# Revit family: Axis-Jet-СI
name_source: partatom
category: Оборудование
units: mm (PartAtom-declared; Revit-internal decimal feet)

## family parameters
Всегда вертикально = Да
Классификация = Нет
На основе рабочей плоскости = Нет
Общий = Нет
При загрузке вырезать с полостями = Нет
Размер круглого соединителя = Использовать диаметр
Тип детали = Нормальный
Точка принадлежности помещению = Нет

## types (126) — shared parameters
00_20_Manufacturer = BLAUBERG
00_20_Name = Jet axial fan
Casing Material = Metal, painted, grey, matt RAL 7040
E1 = 830 мм
Frequency = 50 Гц
Load Classification = HVAC
Maintenance zone material = <По категории>
Number of Fase = 3
Thrust = 0.00 Н
Voltage = 400 В
Изготовитель = BLAUBERG
zero-valued in all types: Отметка по умолчанию

## per-type parameters (varying)
- Axis-Jet-СI-315-2-U: 00_20_Type=Axis-Jet-СI-315-2-U; A=302 мм; A1=342 мм; B=355 мм; D=414 мм; D1=394 мм; D2=294 мм; Dy=315 мм; H=425 мм; Height=425 мм; L=1654 мм; L1=1763 мм; Length=1763 мм; Maximum Air Flow=4520.0 м³/ч; Motor=Motor : Motor_315; Power=550 Вт; R=207 мм; Type R=Нет; Weight=40.00 кг; Width=414 мм; d1=9 мм; dn=319 мм; k=40 мм; l=109 мм; r=158 мм; t=104 мм
- Axis-Jet-CI-630-2/4-U: 00_20_Type=Axis-Jet-CI-630-2/4-U; A=550 мм; A1=600 мм; B=710 мм; D=733 мм; D1=713 мм; D2=613 мм; Dy=630 мм; H=748 мм; Height=748 мм; L=2193 мм; L1=2357 мм; Length=2357 мм; Maximum Air Flow=31500.0 м³/ч; Motor=Motor : Motor_630; Power=12000 Вт; R=367 мм; Type R=Нет; Weight=245.00 кг; Width=733 мм; d1=13 мм; dn=634 мм; k=50 мм; l=164 мм; r=315 мм; t=183 мм
- Axis-Jet-СI-315-2-R: 00_20_Type=Axis-Jet-СI-315-2-R; A=302 мм; A1=342 мм; B=355 мм; D=414 мм; D1=394 мм; D2=294 мм; Dy=315 мм; H=425 мм; Height=425 мм; L=1654 мм; L1=1763 мм; Length=1872 мм; Maximum Air Flow=4190.0 м³/ч; Motor=Motor : Motor_315; Power=550 Вт; R=207 мм; Type R=Да; Weight=40.00 кг; Width=414 мм; d1=9 мм; dn=319 мм; k=40 мм; l=109 мм; r=158 мм; t=104 мм
- Axis-Jet-СI-355-2-U: 00_20_Type=Axis-Jet-СI-355-2-U; A=302 мм; A1=342 мм; B=420 мм; D=467 мм; D1=447 мм; D2=347 мм; Dy=355 мм; H=482 мм; Height=482 мм; L=1954 мм; L1=2079 мм; Length=2079 мм; Maximum Air Flow=5830.0 м³/ч; Motor=Motor : Motor_355; Power=750 Вт; R=234 мм; Type R=Нет; Weight=50.00 кг; Width=467 мм; d1=9 мм; dn=359 мм; k=40 мм; l=125 мм; r=178 мм; t=117 мм
- Axis-Jet-СI-355-2-R: 00_20_Type=Axis-Jet-СI-355-2-R; A=302 мм; A1=342 мм; B=420 мм; D=467 мм; D1=447 мм; D2=347 мм; Dy=355 мм; H=482 мм; Height=482 мм; L=1954 мм; L1=2079 мм; Length=2204 мм; Maximum Air Flow=5810.0 м³/ч; Motor=Motor : Motor_355; Power=1100 Вт; R=234 мм; Type R=Да; Weight=50.00 кг; Width=467 мм; d1=9 мм; dn=359 мм; k=40 мм; l=125 мм; r=178 мм; t=117 мм
- Axis-Jet-СI-400-2-U: 00_20_Type=Axis-Jet-СI-400-2-U; A=351 мм; A1=401 мм; B=460 мм; D=515 мм; D1=495 мм; D2=395 мм; Dy=400 мм; H=525 мм; Height=525 мм; L=2004 мм; L1=2129 мм; Length=2129 мм; Maximum Air Flow=8500.0 м³/ч; Motor=Motor : Motor_400; Power=1100 Вт; R=258 мм; Type R=Нет; Weight=65.00 кг; Width=515 мм; d1=13 мм; dn=404 мм; k=50 мм; l=125 мм; r=200 мм; t=129 мм
- Axis-Jet-СI-400-2-R: 00_20_Type=Axis-Jet-СI-400-2-R; A=351 мм; A1=401 мм; B=460 мм; D=515 мм; D1=495 мм; D2=395 мм; Dy=400 мм; H=525 мм; Height=525 мм; L=2004 мм; L1=2129 мм; Length=2254 мм; Maximum Air Flow=8290.0 м³/ч; Motor=Motor : Motor_400; Power=1500 Вт; R=258 мм; Type R=Да; Weight=65.00 кг; Width=515 мм; d1=13 мм; dn=404 мм; k=50 мм; l=125 мм; r=200 мм; t=129 мм
- Axis-Jet-СI-450-2-U: 00_20_Type=Axis-Jet-СI-450-2-U; A=351 мм; A1=401 мм; B=500 мм; D=565 мм; D1=545 мм; D2=445 мм; Dy=450 мм; H=575 мм; Height=575 мм; L=2004 мм; L1=2129 мм; Length=2129 мм; Maximum Air Flow=10400.0 м³/ч; Motor=Motor : Motor_450; Power=1500 Вт; R=283 мм; Type R=Нет; Weight=85.00 кг; Width=565 мм; d1=13 мм; dn=454 мм; k=50 мм; l=125 мм; r=225 мм; t=141 мм
- Axis-Jet-СI-450-2-R: 00_20_Type=Axis-Jet-СI-450-2-R; A=351 мм; A1=401 мм; B=500 мм; D=565 мм; D1=545 мм; D2=445 мм; Dy=450 мм; H=575 мм; Height=575 мм; L=2004 мм; L1=2129 мм; Length=2254 мм; Maximum Air Flow=9280.0 м³/ч; Motor=Motor : Motor_450; Power=1500 Вт; R=283 мм; Type R=Да; Weight=85.00 кг; Width=565 мм; d1=13 мм; dn=454 мм; k=50 мм; l=125 мм; r=225 мм; t=141 мм
- Axis-Jet-СI-500-2/4-U: 00_20_Type=Axis-Jet-СI-500-2/4-U; A=371 мм; A1=421 мм; B=580 мм; D=603 мм; D1=583 мм; D2=483 мм; Dy=500 мм; H=620 мм; Height=620 мм; L=2004 мм; L1=2145 мм; Length=2145 мм; Maximum Air Flow=16200.0 м³/ч; Motor=Motor : Motor_500; Power=3100 Вт; R=302 мм; Type R=Нет; Weight=110.00 кг; Width=603 мм; d1=13 мм; dn=504 мм; k=50 мм; l=141 мм; r=250 мм; t=151 мм
- Axis-Jet-CI-500-2/4-R: 00_20_Type=Axis-Jet-CI-500-2/4-R; A=371 мм; A1=421 мм; B=580 мм; D=603 мм; D1=583 мм; D2=483 мм; Dy=500 мм; H=620 мм; Height=620 мм; L=2004 мм; L1=2145 мм; Length=2286 мм; Maximum Air Flow=14500.0 м³/ч; Motor=Motor : Motor_500; Power=3100 Вт; R=302 мм; Type R=Да; Weight=110.00 кг; Width=603 мм; d1=13 мм; dn=504 мм; k=50 мм; l=141 мм; r=250 мм; t=151 мм
- Axis-Jet-CI-560-2/4-U: 00_20_Type=Axis-Jet-CI-560-2/4-U; A=446 мм; A1=496 мм; B=620 мм; D=663 мм; D1=643 мм; D2=543 мм; Dy=560 мм; H=678 мм; Height=678 мм; L=2093 мм; L1=2247 мм; Length=2247 мм; Maximum Air Flow=20200.0 м³/ч; Motor=Motor : Motor_560; Power=4400 Вт; R=332 мм; Type R=Нет; Weight=155.00 кг; Width=663 мм; d1=13 мм; dn=564 мм; k=50 мм; l=154 мм; r=280 мм; t=166 мм
- Axis-Jet-CI-560-2/4-R: 00_20_Type=Axis-Jet-CI-560-2/4-R; A=446 мм; A1=496 мм; B=620 мм; D=663 мм; D1=643 мм; D2=543 мм; Dy=560 мм; H=678 мм; Height=678 мм; L=2093 мм; L1=2247 мм; Length=2401 мм; Maximum Air Flow=16800.0 м³/ч; Motor=Motor : Motor_560; Power=4400 Вт; R=332 мм; Type R=Да; Weight=155.00 кг; Width=663 мм; d1=13 мм; dn=564 мм; k=50 мм; l=154 мм; r=280 мм; t=166 мм
- Axis-Jet-CI-630-2/4-R: 00_20_Type=Axis-Jet-CI-630-2/4-R; A=550 мм; A1=600 мм; B=710 мм; D=733 мм; D1=713 мм; D2=613 мм; Dy=630 мм; H=748 мм; Height=748 мм; L=2193 мм; L1=2357 мм; Length=2521 мм; Maximum Air Flow=26700.0 м³/ч; Motor=Motor : Motor_630; Power=12000 Вт; R=367 мм; Type R=Да; Weight=245.00 кг; Width=733 мм; d1=13 мм; dn=634 мм; k=50 мм; l=164 мм; r=315 мм; t=183 мм
- Axis-Jet-СI-315-2-U-300/2: 00_20_Type=Axis-Jet-СI-315-2-U-300/2; A=302 мм; A1=342 мм; B=355 мм; D=414 мм; D1=394 мм; D2=294 мм; Dy=315 мм; H=425 мм; Height=425 мм; L=1654 мм; L1=1763 мм; Length=1763 мм; Maximum Air Flow=4520.0 м³/ч; Motor=Motor : Motor_315; Power=550 Вт; R=207 мм; Type R=Нет; Weight=40.00 кг; Width=414 мм; d1=9 мм; dn=319 мм; k=40 мм; l=109 мм; r=158 мм; t=104 мм
- Axis-Jet-СI-315-2-U-400/2: 00_20_Type=Axis-Jet-СI-315-2-U-400/2; A=302 мм; A1=342 мм; B=355 мм; D=414 мм; D1=394 мм; D2=294 мм; Dy=315 мм; H=425 мм; Height=425 мм; L=1654 мм; L1=1763 мм; Length=1763 мм; Maximum Air Flow=3250.0 м³/ч; Motor=Motor : Motor_315; Power=550 Вт; R=207 мм; Type R=Нет; Weight=40.00 кг; Width=414 мм; d1=9 мм; dn=319 мм; k=40 мм; l=109 мм; r=158 мм; t=104 мм
- Axis-Jet-СI-315M-2-U: 00_20_Type=Axis-Jet-СI-315M-2-U; A=302 мм; A1=342 мм; B=355 мм; D=414 мм; D1=394 мм; D2=294 мм; Dy=315 мм; H=425 мм; Height=425 мм; L=1654 мм; L1=1763 мм; Length=1763 мм; Maximum Air Flow=4990.0 м³/ч; Motor=Motor : Motor_315; Power=750 Вт; R=207 мм; Type R=Нет; Weight=40.00 кг; Width=414 мм; d1=9 мм; dn=319 мм; k=40 мм; l=109 мм; r=158 мм; t=104 мм
- Axis-Jet-СI-315M-2-U-300/2: 00_20_Type=Axis-Jet-СI-315M-2-U-300/2; A=302 мм; A1=342 мм; B=355 мм; D=414 мм; D1=394 мм; D2=294 мм; Dy=315 мм; H=425 мм; Height=425 мм; L=1654 мм; L1=1763 мм; Length=1763 мм; Maximum Air Flow=4990.0 м³/ч; Motor=Motor : Motor_315; Power=750 Вт; R=207 мм; Type R=Нет; Weight=40.00 кг; Width=414 мм; d1=9 мм; dn=319 мм; k=40 мм; l=109 мм; r=158 мм; t=104 мм
- Axis-Jet-СI-315M-2-U-400/2: 00_20_Type=Axis-Jet-СI-315M-2-U-400/2; A=302 мм; A1=342 мм; B=355 мм; D=414 мм; D1=394 мм; D2=294 мм; Dy=315 мм; H=425 мм; Height=425 мм; L=1654 мм; L1=1763 мм; Length=1763 мм; Maximum Air Flow=3590.0 м³/ч; Motor=Motor : Motor_315; Power=750 Вт; R=207 мм; Type R=Нет; Weight=40.00 кг; Width=414 мм; d1=9 мм; dn=319 мм; k=40 мм; l=109 мм; r=158 мм; t=104 мм
- Axis-Jet-СI-315-2/4-U: 00_20_Type=Axis-Jet-СI-315-2/4-U; A=302 мм; A1=342 мм; B=355 мм; D=414 мм; D1=394 мм; D2=294 мм; Dy=315 мм; H=425 мм; Height=425 мм; L=1654 мм; L1=1763 мм; Length=1763 мм; Maximum Air Flow=4520.0 м³/ч; Motor=Motor : Motor_315; Power=550 Вт; R=207 мм; Type R=Нет; Weight=40.00 кг; Width=414 мм; d1=9 мм; dn=319 мм; k=40 мм; l=109 мм; r=158 мм; t=104 мм
- Axis-Jet-СI-315-2/4-U-300/2: 00_20_Type=Axis-Jet-СI-315-2/4-U-300/2; A=302 мм; A1=342 мм; B=355 мм; D=414 мм; D1=394 мм; D2=294 мм; Dy=315 мм; H=425 мм; Height=425 мм; L=1654 мм; L1=1763 мм; Length=1763 мм; Maximum Air Flow=4520.0 м³/ч; Motor=Motor : Motor_315; Power=550 Вт; R=207 мм; Type R=Нет; Weight=40.00 кг; Width=414 мм; d1=9 мм; dn=319 мм; k=40 мм; l=109 мм; r=158 мм; t=104 мм
- Axis-Jet-СI-315-2/4-U-400/2: 00_20_Type=Axis-Jet-СI-315-2/4-U-400/2; A=302 мм; A1=342 мм; B=355 мм; D=414 мм; D1=394 мм; D2=294 мм; Dy=315 мм; H=425 мм; Height=425 мм; L=1654 мм; L1=1763 мм; Length=1763 мм; Maximum Air Flow=3250.0 м³/ч; Motor=Motor : Motor_315; Power=550 Вт; R=207 мм; Type R=Нет; Weight=40.00 кг; Width=414 мм; d1=9 мм; dn=319 мм; k=40 мм; l=109 мм; r=158 мм; t=104 мм
- Axis-Jet-СI-315M-2/4-U: 00_20_Type=Axis-Jet-СI-315M-2/4-U; A=302 мм; A1=342 мм; B=355 мм; D=414 мм; D1=394 мм; D2=294 мм; Dy=315 мм; H=425 мм; Height=425 мм; L=1654 мм; L1=1763 мм; Length=1763 мм; Maximum Air Flow=4990.0 м³/ч; Motor=Motor : Motor_315; Power=800 Вт; R=207 мм; Type R=Нет; Weight=40.00 кг; Width=414 мм; d1=9 мм; dn=319 мм; k=40 мм; l=109 мм; r=158 мм; t=104 мм
- Axis-Jet-СI-315M-2/4-U-300/2: 00_20_Type=Axis-Jet-СI-315M-2/4-U-300/2; A=302 мм; A1=342 мм; B=355 мм; D=414 мм; D1=394 мм; D2=294 мм; Dy=315 мм; H=425 мм; Height=425 мм; L=1654 мм; L1=1763 мм; Length=1763 мм; Maximum Air Flow=4990.0 м³/ч; Motor=Motor : Motor_315; Power=800 Вт; R=207 мм; Type R=Нет; Weight=40.00 кг; Width=414 мм; d1=9 мм; dn=319 мм; k=40 мм; l=109 мм; r=158 мм; t=104 мм
- Axis-Jet-СI-315M-2/4-U-400/2: 00_20_Type=Axis-Jet-СI-315M-2/4-U-400/2; A=302 мм; A1=342 мм; B=355 мм; D=414 мм; D1=394 мм; D2=294 мм; Dy=315 мм; H=425 мм; Height=425 мм; L=1654 мм; L1=1763 мм; Length=1763 мм; Maximum Air Flow=3590.0 м³/ч; Motor=Motor : Motor_315; Power=800 Вт; R=207 мм; Type R=Нет; Weight=40.00 кг; Width=414 мм; d1=9 мм; dn=319 мм; k=40 мм; l=109 мм; r=158 мм; t=104 мм
- Axis-Jet-СI-315-2-R-300/2: 00_20_Type=Axis-Jet-СI-315-2-R-300/2; A=302 мм; A1=342 мм; B=355 мм; D=414 мм; D1=394 мм; D2=294 мм; Dy=315 мм; H=425 мм; Height=425 мм; L=1654 мм; L1=1763 мм; Length=1872 мм; Maximum Air Flow=4190.0 м³/ч; Motor=Motor : Motor_315; Power=550 Вт; R=207 мм; Type R=Да; Weight=40.00 кг; Width=414 мм; d1=9 мм; dn=319 мм; k=40 мм; l=109 мм; r=158 мм; t=104 мм
- Axis-Jet-СI-315-2-R-400/2: 00_20_Type=Axis-Jet-СI-315-2-R-400/2; A=302 мм; A1=342 мм; B=355 мм; D=414 мм; D1=394 мм; D2=294 мм; Dy=315 мм; H=425 мм; Height=425 мм; L=1654 мм; L1=1763 мм; Length=1872 мм; Maximum Air Flow=3010.0 м³/ч; Motor=Motor : Motor_315; Power=550 Вт; R=207 мм; Type R=Да; Weight=40.00 кг; Width=414 мм; d1=9 мм; dn=319 мм; k=40 мм; l=109 мм; r=158 мм; t=104 мм
- Axis-Jet-СI-315-2/4-R-300/2: 00_20_Type=Axis-Jet-СI-315-2/4-R-300/2; A=302 мм; A1=342 мм; B=355 мм; D=414 мм; D1=394 мм; D2=294 мм; Dy=315 мм; H=425 мм; Height=425 мм; L=1654 мм; L1=1763 мм; Length=1872 мм; Maximum Air Flow=4180.0 м³/ч; Motor=Motor : Motor_315; Power=550 Вт; R=207 мм; Type R=Да; Weight=40.00 кг; Width=414 мм; d1=9 мм; dn=319 мм; k=40 мм; l=109 мм; r=158 мм; t=104 мм
- Axis-Jet-СI-315-2/4-R-400/2: 00_20_Type=Axis-Jet-СI-315-2/4-R-400/2; A=302 мм; A1=342 мм; B=355 мм; D=414 мм; D1=394 мм; D2=294 мм; Dy=315 мм; H=425 мм; Height=425 мм; L=1654 мм; L1=1763 мм; Length=1872 мм; Maximum Air Flow=3010.0 м³/ч; Motor=Motor : Motor_315; Power=550 Вт; R=207 мм; Type R=Да; Weight=40.00 кг; Width=414 мм; d1=9 мм; dn=319 мм; k=40 мм; l=109 мм; r=158 мм; t=104 мм
- Axis-Jet-СI-355-2-U-300/2: 00_20_Type=Axis-Jet-СI-355-2-U-300/2; A=302 мм; A1=342 мм; B=420 мм; D=467 мм; D1=447 мм; D2=347 мм; Dy=355 мм; H=482 мм; Height=482 мм; L=1954 мм; L1=2079 мм; Length=2079 мм; Maximum Air Flow=5830.0 м³/ч; Motor=Motor : Motor_355; Power=750 Вт; R=234 мм; Type R=Нет; Weight=50.00 кг; Width=467 мм; d1=9 мм; dn=359 мм; k=40 мм; l=125 мм; r=178 мм; t=117 мм
- Axis-Jet-СI-355-2-U-400/2: 00_20_Type=Axis-Jet-СI-355-2-U-400/2; A=302 мм; A1=342 мм; B=420 мм; D=467 мм; D1=447 мм; D2=347 мм; Dy=355 мм; H=482 мм; Height=482 мм; L=1954 мм; L1=2079 мм; Length=2079 мм; Maximum Air Flow=4880.0 м³/ч; Motor=Motor : Motor_355; Power=750 Вт; R=234 мм; Type R=Нет; Weight=50.00 кг; Width=467 мм; d1=9 мм; dn=359 мм; k=40 мм; l=125 мм; r=178 мм; t=117 мм
- Axis-Jet-СI-355M-2-U: 00_20_Type=Axis-Jet-СI-355M-2-U; A=302 мм; A1=342 мм; B=420 мм; D=467 мм; D1=447 мм; D2=347 мм; Dy=355 мм; H=482 мм; Height=482 мм; L=1954 мм; L1=2079 мм; Length=2079 мм; Maximum Air Flow=6740.0 м³/ч; Motor=Motor : Motor_355; Power=11000 Вт; R=234 мм; Type R=Нет; Weight=50.00 кг; Width=467 мм; d1=9 мм; dn=359 мм; k=40 мм; l=125 мм; r=178 мм; t=117 мм
- Axis-Jet-СI-355M-2-U-300/2: 00_20_Type=Axis-Jet-СI-355M-2-U-300/2; A=302 мм; A1=342 мм; B=420 мм; D=467 мм; D1=447 мм; D2=347 мм; Dy=355 мм; H=482 мм; Height=482 мм; L=1954 мм; L1=2079 мм; Length=2079 мм; Maximum Air Flow=6740.0 м³/ч; Motor=Motor : Motor_355; Power=11000 Вт; R=234 мм; Type R=Нет; Weight=50.00 кг; Width=467 мм; d1=9 мм; dn=359 мм; k=40 мм; l=125 мм; r=178 мм; t=117 мм
- Axis-Jet-СI-355M-2-U-400/2: 00_20_Type=Axis-Jet-СI-355M-2-U-400/2; A=302 мм; A1=342 мм; B=420 мм; D=467 мм; D1=447 мм; D2=347 мм; Dy=355 мм; H=482 мм; Height=482 мм; L=1954 мм; L1=2079 мм; Length=2079 мм; Maximum Air Flow=5360.0 м³/ч; Motor=Motor : Motor_355; Power=11000 Вт; R=234 мм; Type R=Нет; Weight=50.00 кг; Width=467 мм; d1=9 мм; dn=359 мм; k=40 мм; l=125 мм; r=178 мм; t=117 мм
- Axis-Jet-СI-355-2/4-U: 00_20_Type=Axis-Jet-СI-355-2/4-U; A=302 мм; A1=342 мм; B=420 мм; D=467 мм; D1=447 мм; D2=347 мм; Dy=355 мм; H=482 мм; Height=482 мм; L=1954 мм; L1=2079 мм; Length=2079 мм; Maximum Air Flow=5830.0 м³/ч; Motor=Motor : Motor_355; Power=800 Вт; R=234 мм; Type R=Нет; Weight=50.00 кг; Width=467 мм; d1=9 мм; dn=359 мм; k=40 мм; l=125 мм; r=178 мм; t=117 мм
- Axis-Jet-СI-355-2/4-U-300/2: 00_20_Type=Axis-Jet-СI-355-2/4-U-300/2; A=302 мм; A1=342 мм; B=420 мм; D=467 мм; D1=447 мм; D2=347 мм; Dy=355 мм; H=482 мм; Height=482 мм; L=1954 мм; L1=2079 мм; Length=2079 мм; Maximum Air Flow=5830.0 м³/ч; Motor=Motor : Motor_355; Power=800 Вт; R=234 мм; Type R=Нет; Weight=50.00 кг; Width=467 мм; d1=9 мм; dn=359 мм; k=40 мм; l=125 мм; r=178 мм; t=117 мм
- Axis-Jet-СI-355-2/4-U-400/2: 00_20_Type=Axis-Jet-СI-355-2/4-U-400/2; A=302 мм; A1=342 мм; B=420 мм; D=467 мм; D1=447 мм; D2=347 мм; Dy=355 мм; H=482 мм; Height=482 мм; L=1954 мм; L1=2079 мм; Length=2079 мм; Maximum Air Flow=4880.0 м³/ч; Motor=Motor : Motor_355; Power=800 Вт; R=234 мм; Type R=Нет; Weight=50.00 кг; Width=467 мм; d1=9 мм; dn=359 мм; k=40 мм; l=125 мм; r=178 мм; t=117 мм
- Axis-Jet-СI-355M-2/4-U: 00_20_Type=Axis-Jet-СI-355M-2/4-U; A=302 мм; A1=342 мм; B=420 мм; D=467 мм; D1=447 мм; D2=347 мм; Dy=355 мм; H=482 мм; Height=482 мм; L=1954 мм; L1=2079 мм; Length=2079 мм; Maximum Air Flow=6740.0 м³/ч; Motor=Motor : Motor_355; Power=1100 Вт; R=234 мм; Type R=Нет; Weight=50.00 кг; Width=467 мм; d1=9 мм; dn=359 мм; k=40 мм; l=125 мм; r=178 мм; t=117 мм
- Axis-Jet-СI-355M-2/4-U-300/2: 00_20_Type=Axis-Jet-СI-355M-2/4-U-300/2; A=302 мм; A1=342 мм; B=420 мм; D=467 мм; D1=447 мм; D2=347 мм; Dy=355 мм; H=482 мм; Height=482 мм; L=1954 мм; L1=2079 мм; Length=2079 мм; Maximum Air Flow=6740.0 м³/ч; Motor=Motor : Motor_355; Power=1100 Вт; R=234 мм; Type R=Нет; Weight=50.00 кг; Width=467 мм; d1=9 мм; dn=359 мм; k=40 мм; l=125 мм; r=178 мм; t=117 мм
- Axis-Jet-СI-355M-2/4-U-400/2: 00_20_Type=Axis-Jet-СI-355M-2/4-U-400/2; A=302 мм; A1=342 мм; B=420 мм; D=467 мм; D1=447 мм; D2=347 мм; Dy=355 мм; H=482 мм; Height=482 мм; L=1954 мм; L1=2079 мм; Length=2079 мм; Maximum Air Flow=5360.0 м³/ч; Motor=Motor : Motor_355; Power=1100 Вт; R=234 мм; Type R=Нет; Weight=50.00 кг; Width=467 мм; d1=9 мм; dn=359 мм; k=40 мм; l=125 мм; r=178 мм; t=117 мм
- Axis-Jet-СI-315-2/4-R: 00_20_Type=Axis-Jet-СI-315-2/4-R; A=302 мм; A1=342 мм; B=355 мм; D=414 мм; D1=394 мм; D2=294 мм; Dy=315 мм; H=425 мм; Height=425 мм; L=1654 мм; L1=1763 мм; Length=1872 мм; Maximum Air Flow=4180.0 м³/ч; Motor=Motor : Motor_315; Power=550 Вт; R=207 мм; Type R=Да; Weight=40.00 кг; Width=414 мм; d1=9 мм; dn=319 мм; k=40 мм; l=109 мм; r=158 мм; t=104 мм
- Axis-Jet-СI-355-2-R-300/2: 00_20_Type=Axis-Jet-СI-355-2-R-300/2; A=302 мм; A1=342 мм; B=420 мм; D=467 мм; D1=447 мм; D2=347 мм; Dy=355 мм; H=482 мм; Height=482 мм; L=1954 мм; L1=2079 мм; Length=2204 мм; Maximum Air Flow=5810.0 м³/ч; Motor=Motor : Motor_355; Power=1100 Вт; R=234 мм; Type R=Да; Weight=50.00 кг; Width=467 мм; d1=9 мм; dn=359 мм; k=40 мм; l=125 мм; r=178 мм; t=117 мм
- Axis-Jet-СI-355-2-R-400/2: 00_20_Type=Axis-Jet-СI-355-2-R-400/2; A=302 мм; A1=342 мм; B=420 мм; D=467 мм; D1=447 мм; D2=347 мм; Dy=355 мм; H=482 мм; Height=482 мм; L=1954 мм; L1=2079 мм; Length=2204 мм; Maximum Air Flow=5160.0 м³/ч; Motor=Motor : Motor_355; Power=1100 Вт; R=234 мм; Type R=Да; Weight=50.00 кг; Width=467 мм; d1=9 мм; dn=359 мм; k=40 мм; l=125 мм; r=178 мм; t=117 мм
- Axis-Jet-СI-355-2/4-R: 00_20_Type=Axis-Jet-СI-355-2/4-R; A=302 мм; A1=342 мм; B=420 мм; D=467 мм; D1=447 мм; D2=347 мм; Dy=355 мм; H=482 мм; Height=482 мм; L=1954 мм; L1=2079 мм; Length=2204 мм; Maximum Air Flow=5810.0 м³/ч; Motor=Motor : Motor_355; Power=1100 Вт; R=234 мм; Type R=Да; Weight=50.00 кг; Width=467 мм; d1=9 мм; dn=359 мм; k=40 мм; l=125 мм; r=178 мм; t=117 мм
- Axis-Jet-СI-355-2/4-R-300/2: 00_20_Type=Axis-Jet-СI-355-2/4-R-300/2; A=302 мм; A1=342 мм; B=420 мм; D=467 мм; D1=447 мм; D2=347 мм; Dy=355 мм; H=482 мм; Height=482 мм; L=1954 мм; L1=2079 мм; Length=2204 мм; Maximum Air Flow=5810.0 м³/ч; Motor=Motor : Motor_355; Power=1100 Вт; R=234 мм; Type R=Да; Weight=50.00 кг; Width=467 мм; d1=9 мм; dn=359 мм; k=40 мм; l=125 мм; r=178 мм; t=117 мм
- Axis-Jet-СI-355-2/4-R-400/2: 00_20_Type=Axis-Jet-СI-355-2/4-R-400/2; A=302 мм; A1=342 мм; B=420 мм; D=467 мм; D1=447 мм; D2=347 мм; Dy=355 мм; H=482 мм; Height=482 мм; L=1954 мм; L1=2079 мм; Length=2204 мм; Maximum Air Flow=5160.0 м³/ч; Motor=Motor : Motor_355; Power=1100 Вт; R=234 мм; Type R=Да; Weight=50.00 кг; Width=467 мм; d1=9 мм; dn=359 мм; k=40 мм; l=125 мм; r=178 мм; t=117 мм
- Axis-Jet-СI-400-2-U-300/2: 00_20_Type=Axis-Jet-СI-400-2-U-300/2; A=351 мм; A1=401 мм; B=460 мм; D=515 мм; D1=495 мм; D2=395 мм; Dy=400 мм; H=525 мм; Height=525 мм; L=2004 мм; L1=2129 мм; Length=2129 мм; Maximum Air Flow=8500.0 м³/ч; Motor=Motor : Motor_400; Power=1100 Вт; R=258 мм; Type R=Нет; Weight=65.00 кг; Width=515 мм; d1=13 мм; dn=404 мм; k=50 мм; l=125 мм; r=200 мм; t=129 мм
- Axis-Jet-СI-400-2-U-400/2: 00_20_Type=Axis-Jet-СI-400-2-U-400/2; A=351 мм; A1=401 мм; B=460 мм; D=515 мм; D1=495 мм; D2=395 мм; Dy=400 мм; H=525 мм; Height=525 мм; L=2004 мм; L1=2129 мм; Length=2129 мм; Maximum Air Flow=6970.0 м³/ч; Motor=Motor : Motor_400; Power=1100 Вт; R=258 мм; Type R=Нет; Weight=65.00 кг; Width=515 мм; d1=13 мм; dn=404 мм; k=50 мм; l=125 мм; r=200 мм; t=129 мм
- Axis-Jet-СI-400M-2-U: 00_20_Type=Axis-Jet-СI-400M-2-U; A=351 мм; A1=401 мм; B=460 мм; D=515 мм; D1=495 мм; D2=395 мм; Dy=400 мм; H=525 мм; Height=525 мм; L=2004 мм; L1=2129 мм; Length=2129 мм; Maximum Air Flow=9870.0 м³/ч; Motor=Motor : Motor_400; Power=2200 Вт; R=258 мм; Type R=Нет; Weight=65.00 кг; Width=515 мм; d1=13 мм; dn=404 мм; k=50 мм; l=125 мм; r=200 мм; t=129 мм
- Axis-Jet-СI-400M-2-U-300/2: 00_20_Type=Axis-Jet-СI-400M-2-U-300/2; A=351 мм; A1=401 мм; B=460 мм; D=515 мм; D1=495 мм; D2=395 мм; Dy=400 мм; H=525 мм; Height=525 мм; L=2004 мм; L1=2129 мм; Length=2129 мм; Maximum Air Flow=9870.0 м³/ч; Motor=Motor : Motor_400; Power=2200 Вт; R=258 мм; Type R=Нет; Weight=65.00 кг; Width=515 мм; d1=13 мм; dn=404 мм; k=50 мм; l=125 мм; r=200 мм; t=129 мм
- Axis-Jet-СI-400M-2-U-400/2: 00_20_Type=Axis-Jet-СI-400M-2-U-400/2; A=351 мм; A1=401 мм; B=460 мм; D=515 мм; D1=495 мм; D2=395 мм; Dy=400 мм; H=525 мм; Height=525 мм; L=2004 мм; L1=2129 мм; Length=2129 мм; Maximum Air Flow=8500.0 м³/ч; Motor=Motor : Motor_400; Power=2200 Вт; R=258 мм; Type R=Нет; Weight=65.00 кг; Width=515 мм; d1=13 мм; dn=404 мм; k=50 мм; l=125 мм; r=200 мм; t=129 мм
- Axis-Jet-СI-400-2/4-U: 00_20_Type=Axis-Jet-СI-400-2/4-U; A=351 мм; A1=401 мм; B=460 мм; D=515 мм; D1=495 мм; D2=395 мм; Dy=400 мм; H=525 мм; Height=525 мм; L=2004 мм; L1=2129 мм; Length=2129 мм; Maximum Air Flow=8500.0 м³/ч; Motor=Motor : Motor_400; Power=1100 Вт; R=258 мм; Type R=Нет; Weight=65.00 кг; Width=515 мм; d1=13 мм; dn=404 мм; k=50 мм; l=125 мм; r=200 мм; t=129 мм
- Axis-Jet-СI-400-2/4-U-300/2: 00_20_Type=Axis-Jet-СI-400-2/4-U-300/2; A=351 мм; A1=401 мм; B=460 мм; D=515 мм; D1=495 мм; D2=395 мм; Dy=400 мм; H=525 мм; Height=525 мм; L=2004 мм; L1=2129 мм; Length=2129 мм; Maximum Air Flow=8500.0 м³/ч; Motor=Motor : Motor_400; Power=1100 Вт; R=258 мм; Type R=Нет; Weight=65.00 кг; Width=515 мм; d1=13 мм; dn=404 мм; k=50 мм; l=125 мм; r=200 мм; t=129 мм
- Axis-Jet-СI-400-2/4-U-400/2: 00_20_Type=Axis-Jet-СI-400-2/4-U-400/2; A=351 мм; A1=401 мм; B=460 мм; D=515 мм; D1=495 мм; D2=395 мм; Dy=400 мм; H=525 мм; Height=525 мм; L=2004 мм; L1=2129 мм; Length=2129 мм; Maximum Air Flow=6970.0 м³/ч; Motor=Motor : Motor_400; Power=1100 Вт; R=258 мм; Type R=Нет; Weight=65.00 кг; Width=515 мм; d1=13 мм; dn=404 мм; k=50 мм; l=125 мм; r=200 мм; t=129 мм
- Axis-Jet-СI-400M-2/4-U: 00_20_Type=Axis-Jet-СI-400M-2/4-U; A=351 мм; A1=401 мм; B=460 мм; D=515 мм; D1=495 мм; D2=395 мм; Dy=400 мм; H=525 мм; Height=525 мм; L=2004 мм; L1=2129 мм; Length=2129 мм; Maximum Air Flow=9870.0 м³/ч; Motor=Motor : Motor_400; Power=2200 Вт; R=258 мм; Type R=Нет; Weight=65.00 кг; Width=515 мм; d1=13 мм; dn=404 мм; k=50 мм; l=125 мм; r=200 мм; t=129 мм
- Axis-Jet-СI-400M-2/4-U-300/2: 00_20_Type=Axis-Jet-СI-400M-2/4-U-300/2; A=351 мм; A1=401 мм; B=460 мм; D=515 мм; D1=495 мм; D2=395 мм; Dy=400 мм; H=525 мм; Height=525 мм; L=2004 мм; L1=2129 мм; Length=2129 мм; Maximum Air Flow=9870.0 м³/ч; Motor=Motor : Motor_400; Power=2200 Вт; R=258 мм; Type R=Нет; Weight=65.00 кг; Width=515 мм; d1=13 мм; dn=404 мм; k=50 мм; l=125 мм; r=200 мм; t=129 мм
- Axis-Jet-СI-400M-2/4-U-400/2: 00_20_Type=Axis-Jet-СI-400M-2/4-U-400/2; A=351 мм; A1=401 мм; B=460 мм; D=515 мм; D1=495 мм; D2=395 мм; Dy=400 мм; H=525 мм; Height=525 мм; L=2004 мм; L1=2129 мм; Length=2129 мм; Maximum Air Flow=8500.0 м³/ч; Motor=Motor : Motor_400; Power=2200 Вт; R=258 мм; Type R=Нет; Weight=65.00 кг; Width=515 мм; d1=13 мм; dn=404 мм; k=50 мм; l=125 мм; r=200 мм; t=129 мм
- Axis-Jet-СI-400-2-R-300/2: 00_20_Type=Axis-Jet-СI-400-2-R-300/2; A=351 мм; A1=401 мм; B=460 мм; D=515 мм; D1=495 мм; D2=395 мм; Dy=400 мм; H=525 мм; Height=525 мм; L=2004 мм; L1=2129 мм; Length=2254 мм; Maximum Air Flow=8290.0 м³/ч; Motor=Motor : Motor_400; Power=1500 Вт; R=258 мм; Type R=Да; Weight=65.00 кг; Width=515 мм; d1=13 мм; dn=404 мм; k=50 мм; l=125 мм; r=200 мм; t=129 мм
- Axis-Jet-СI-400-2-R-400/2: 00_20_Type=Axis-Jet-СI-400-2-R-400/2; A=351 мм; A1=401 мм; B=460 мм; D=515 мм; D1=495 мм; D2=395 мм; Dy=400 мм; H=525 мм; Height=525 мм; L=2004 мм; L1=2129 мм; Length=2254 мм; Maximum Air Flow=7140.0 м³/ч; Motor=Motor : Motor_400; Power=1500 Вт; R=258 мм; Type R=Да; Weight=65.00 кг; Width=515 мм; d1=13 мм; dn=404 мм; k=50 мм; l=125 мм; r=200 мм; t=129 мм
- Axis-Jet-СI-400-2/4-R: 00_20_Type=Axis-Jet-СI-400-2/4-R; A=351 мм; A1=401 мм; B=460 мм; D=515 мм; D1=495 мм; D2=395 мм; Dy=400 мм; H=525 мм; Height=525 мм; L=2004 мм; L1=2129 мм; Length=2254 мм; Maximum Air Flow=8290.0 м³/ч; Motor=Motor : Motor_400; Power=1500 Вт; R=258 мм; Type R=Да; Weight=65.00 кг; Width=515 мм; d1=13 мм; dn=404 мм; k=50 мм; l=125 мм; r=200 мм; t=129 мм
- Axis-Jet-СI-400-2/4-R-300/2: 00_20_Type=Axis-Jet-СI-400-2/4-R-300/2; A=351 мм; A1=401 мм; B=460 мм; D=515 мм; D1=495 мм; D2=395 мм; Dy=400 мм; H=525 мм; Height=525 мм; L=2004 мм; L1=2129 мм; Length=2254 мм; Maximum Air Flow=8290.0 м³/ч; Motor=Motor : Motor_400; Power=1500 Вт; R=258 мм; Type R=Да; Weight=65.00 кг; Width=515 мм; d1=13 мм; dn=404 мм; k=50 мм; l=125 мм; r=200 мм; t=129 мм
- Axis-Jet-СI-400-2/4-R-400/2: 00_20_Type=Axis-Jet-СI-400-2/4-R-400/2; A=351 мм; A1=401 мм; B=460 мм; D=515 мм; D1=495 мм; D2=395 мм; Dy=400 мм; H=525 мм; Height=525 мм; L=2004 мм; L1=2129 мм; Length=2254 мм; Maximum Air Flow=7140.0 м³/ч; Motor=Motor : Motor_400; Power=1500 Вт; R=258 мм; Type R=Да; Weight=65.00 кг; Width=515 мм; d1=13 мм; dn=404 мм; k=50 мм; l=125 мм; r=200 мм; t=129 мм
- Axis-Jet-СI-450-2-U-300/2: 00_20_Type=Axis-Jet-СI-450-2-U-300/2; A=351 мм; A1=401 мм; B=500 мм; D=565 мм; D1=545 мм; D2=445 мм; Dy=450 мм; H=575 мм; Height=575 мм; L=2004 мм; L1=2129 мм; Length=2129 мм; Maximum Air Flow=10400.0 м³/ч; Motor=Motor : Motor_450; Power=1500 Вт; R=283 мм; Type R=Нет; Weight=85.00 кг; Width=565 мм; d1=13 мм; dn=454 мм; k=50 мм; l=125 мм; r=225 мм; t=141 мм
- Axis-Jet-СI-450-2-U-450/2: 00_20_Type=Axis-Jet-СI-450-2-U-450/2; A=351 мм; A1=401 мм; B=500 мм; D=565 мм; D1=545 мм; D2=445 мм; Dy=450 мм; H=575 мм; Height=575 мм; L=2004 мм; L1=2129 мм; Length=2129 мм; Maximum Air Flow=9520.0 м³/ч; Motor=Motor : Motor_450; Power=1500 Вт; R=283 мм; Type R=Нет; Weight=85.00 кг; Width=565 мм; d1=13 мм; dn=454 мм; k=50 мм; l=125 мм; r=225 мм; t=141 мм
- Axis-Jet-СI-450M-2-U: 00_20_Type=Axis-Jet-СI-450M-2-U; A=351 мм; A1=401 мм; B=500 мм; D=565 мм; D1=545 мм; D2=445 мм; Dy=450 мм; H=575 мм; Height=575 мм; L=2004 мм; L1=2129 мм; Length=2129 мм; Maximum Air Flow=12800.0 м³/ч; Motor=Motor : Motor_450; Power=2200 Вт; R=283 мм; Type R=Нет; Weight=85.00 кг; Width=565 мм; d1=13 мм; dn=454 мм; k=50 мм; l=125 мм; r=225 мм; t=141 мм
- Axis-Jet-СI-450M-2-U-300/2: 00_20_Type=Axis-Jet-СI-450M-2-U-300/2; A=351 мм; A1=401 мм; B=500 мм; D=565 мм; D1=545 мм; D2=445 мм; Dy=450 мм; H=575 мм; Height=575 мм; L=2004 мм; L1=2129 мм; Length=2129 мм; Maximum Air Flow=12800.0 м³/ч; Motor=Motor : Motor_450; Power=2200 Вт; R=283 мм; Type R=Нет; Weight=85.00 кг; Width=565 мм; d1=13 мм; dn=454 мм; k=50 мм; l=125 мм; r=225 мм; t=141 мм
- Axis-Jet-СI-450M-2-U-400/2: 00_20_Type=Axis-Jet-СI-450M-2-U-400/2; A=351 мм; A1=401 мм; B=500 мм; D=565 мм; D1=545 мм; D2=445 мм; Dy=450 мм; H=575 мм; Height=575 мм; L=2004 мм; L1=2129 мм; Length=2129 мм; Maximum Air Flow=11600.0 м³/ч; Motor=Motor : Motor_450; Power=2200 Вт; R=283 мм; Type R=Нет; Weight=85.00 кг; Width=565 мм; d1=13 мм; dn=454 мм; k=50 мм; l=125 мм; r=225 мм; t=141 мм
- Axis-Jet-СI-450S-2-U: 00_20_Type=Axis-Jet-СI-450S-2-U; A=351 мм; A1=401 мм; B=500 мм; D=565 мм; D1=545 мм; D2=445 мм; Dy=450 мм; H=575 мм; Height=575 мм; L=2004 мм; L1=2129 мм; Length=2129 мм; Maximum Air Flow=14100.0 м³/ч; Motor=Motor : Motor_450; Power=3000 Вт; R=283 мм; Type R=Нет; Weight=85.00 кг; Width=565 мм; d1=13 мм; dn=454 мм; k=50 мм; l=125 мм; r=225 мм; t=141 мм
- Axis-Jet-СI-450S-2-U-300/2: 00_20_Type=Axis-Jet-СI-450S-2-U-300/2; A=351 мм; A1=401 мм; B=500 мм; D=565 мм; D1=545 мм; D2=445 мм; Dy=450 мм; H=575 мм; Height=575 мм; L=2004 мм; L1=2129 мм; Length=2129 мм; Maximum Air Flow=14100.0 м³/ч; Motor=Motor : Motor_450; Power=3000 Вт; R=283 мм; Type R=Нет; Weight=85.00 кг; Width=565 мм; d1=13 мм; dn=454 мм; k=50 мм; l=125 мм; r=225 мм; t=141 мм
- Axis-Jet-СI-450S-2-U-400/2: 00_20_Type=Axis-Jet-СI-450S-2-U-400/2; A=351 мм; A1=401 мм; B=500 мм; D=565 мм; D1=545 мм; D2=445 мм; Dy=450 мм; H=575 мм; Height=575 мм; L=2004 мм; L1=2129 мм; Length=2129 мм; Maximum Air Flow=12300.0 м³/ч; Motor=Motor : Motor_450; Power=3000 Вт; R=283 мм; Type R=Нет; Weight=85.00 кг; Width=565 мм; d1=13 мм; dn=454 мм; k=50 мм; l=125 мм; r=225 мм; t=141 мм
- Axis-Jet-СI-450-2/4-U: 00_20_Type=Axis-Jet-СI-450-2/4-U; A=351 мм; A1=401 мм; B=500 мм; D=565 мм; D1=545 мм; D2=445 мм; Dy=450 мм; H=575 мм; Height=575 мм; L=2004 мм; L1=2129 мм; Length=2129 мм; Maximum Air Flow=10400.0 м³/ч; Motor=Motor : Motor_450; Power=1500 Вт; R=283 мм; Type R=Нет; Weight=85.00 кг; Width=565 мм; d1=13 мм; dn=454 мм; k=50 мм; l=125 мм; r=225 мм; t=141 мм
- Axis-Jet-СI-450-2/4-U-300/2: 00_20_Type=Axis-Jet-СI-450-2/4-U-300/2; A=351 мм; A1=401 мм; B=500 мм; D=565 мм; D1=545 мм; D2=445 мм; Dy=450 мм; H=575 мм; Height=575 мм; L=2004 мм; L1=2129 мм; Length=2129 мм; Maximum Air Flow=10400.0 м³/ч; Motor=Motor : Motor_450; Power=1500 Вт; R=283 мм; Type R=Нет; Weight=85.00 кг; Width=565 мм; d1=13 мм; dn=454 мм; k=50 мм; l=125 мм; r=225 мм; t=141 мм
- Axis-Jet-СI-450-2/4-U-400/2: 00_20_Type=Axis-Jet-СI-450-2/4-U-400/2; A=351 мм; A1=401 мм; B=500 мм; D=565 мм; D1=545 мм; D2=445 мм; Dy=450 мм; H=575 мм; Height=575 мм; L=2004 мм; L1=2129 мм; Length=2129 мм; Maximum Air Flow=9520.0 м³/ч; Motor=Motor : Motor_450; Power=1500 Вт; R=283 мм; Type R=Нет; Weight=85.00 кг; Width=565 мм; d1=13 мм; dn=454 мм; k=50 мм; l=125 мм; r=225 мм; t=141 мм
- Axis-Jet-СI-450M-2/4-U: 00_20_Type=Axis-Jet-СI-450M-2/4-U; A=351 мм; A1=401 мм; B=500 мм; D=565 мм; D1=545 мм; D2=445 мм; Dy=450 мм; H=575 мм; Height=575 мм; L=2004 мм; L1=2129 мм; Length=2129 мм; Maximum Air Flow=12800.0 м³/ч; Motor=Motor : Motor_450; Power=2200 Вт; R=283 мм; Type R=Нет; Weight=85.00 кг; Width=565 мм; d1=13 мм; dn=454 мм; k=50 мм; l=125 мм; r=225 мм; t=141 мм
- Axis-Jet-СI-450M-2/4-U-300/2: 00_20_Type=Axis-Jet-СI-450M-2/4-U-300/2; A=351 мм; A1=401 мм; B=500 мм; D=565 мм; D1=545 мм; D2=445 мм; Dy=450 мм; H=575 мм; Height=575 мм; L=2004 мм; L1=2129 мм; Length=2129 мм; Maximum Air Flow=12800.0 м³/ч; Motor=Motor : Motor_450; Power=2200 Вт; R=283 мм; Type R=Нет; Weight=85.00 кг; Width=565 мм; d1=13 мм; dn=454 мм; k=50 мм; l=125 мм; r=225 мм; t=141 мм
- Axis-Jet-СI-450M-2/4-U-400/2: 00_20_Type=Axis-Jet-СI-450M-2/4-U-400/2; A=351 мм; A1=401 мм; B=500 мм; D=565 мм; D1=545 мм; D2=445 мм; Dy=450 мм; H=575 мм; Height=575 мм; L=2004 мм; L1=2129 мм; Length=2129 мм; Maximum Air Flow=11600.0 м³/ч; Motor=Motor : Motor_450; Power=2200 Вт; R=283 мм; Type R=Нет; Weight=85.00 кг; Width=565 мм; d1=13 мм; dn=454 мм; k=50 мм; l=125 мм; r=225 мм; t=141 мм
- Axis-Jet-СI-450S-2/4-U: 00_20_Type=Axis-Jet-СI-450S-2/4-U; A=351 мм; A1=401 мм; B=500 мм; D=565 мм; D1=545 мм; D2=445 мм; Dy=450 мм; H=575 мм; Height=575 мм; L=2004 мм; L1=2129 мм; Length=2129 мм; Maximum Air Flow=14100.0 м³/ч; Motor=Motor : Motor_450; Power=3100 Вт; R=283 мм; Type R=Нет; Weight=85.00 кг; Width=565 мм; d1=13 мм; dn=454 мм; k=50 мм; l=125 мм; r=225 мм; t=141 мм
- Axis-Jet-СI-450S-2/4-U-300/2: 00_20_Type=Axis-Jet-СI-450S-2/4-U-300/2; A=351 мм; A1=401 мм; B=500 мм; D=565 мм; D1=545 мм; D2=445 мм; Dy=450 мм; H=575 мм; Height=575 мм; L=2004 мм; L1=2129 мм; Length=2129 мм; Maximum Air Flow=14100.0 м³/ч; Motor=Motor : Motor_450; Power=3100 Вт; R=283 мм; Type R=Нет; Weight=85.00 кг; Width=565 мм; d1=13 мм; dn=454 мм; k=50 мм; l=125 мм; r=225 мм; t=141 мм
- Axis-Jet-СI-450S-2/4-U-400/2: 00_20_Type=Axis-Jet-СI-450S-2/4-U-400/2; A=351 мм; A1=401 мм; B=500 мм; D=565 мм; D1=545 мм; D2=445 мм; Dy=450 мм; H=575 мм; Height=575 мм; L=2004 мм; L1=2129 мм; Length=2129 мм; Maximum Air Flow=12400.0 м³/ч; Motor=Motor : Motor_450; Power=3100 Вт; R=283 мм; Type R=Нет; Weight=85.00 кг; Width=565 мм; d1=13 мм; dn=454 мм; k=50 мм; l=125 мм; r=225 мм; t=141 мм
- Axis-Jet-СI-450-2-R-300/2: 00_20_Type=Axis-Jet-СI-450-2-R-300/2; A=351 мм; A1=401 мм; B=500 мм; D=565 мм; D1=545 мм; D2=445 мм; Dy=450 мм; H=575 мм; Height=575 мм; L=2004 мм; L1=2129 мм; Length=2254 мм; Maximum Air Flow=9280.0 м³/ч; Motor=Motor : Motor_450; Power=1500 Вт; R=283 мм; Type R=Да; Weight=85.00 кг; Width=565 мм; d1=13 мм; dn=454 мм; k=50 мм; l=125 мм; r=225 мм; t=141 мм
- Axis-Jet-СI-450-2/4-R: 00_20_Type=Axis-Jet-СI-450-2/4-R; A=351 мм; A1=401 мм; B=500 мм; D=565 мм; D1=545 мм; D2=445 мм; Dy=450 мм; H=575 мм; Height=575 мм; L=2004 мм; L1=2129 мм; Length=2254 мм; Maximum Air Flow=9280.0 м³/ч; Motor=Motor : Motor_450; Power=1500 Вт; R=283 мм; Type R=Да; Weight=85.00 кг; Width=565 мм; d1=13 мм; dn=454 мм; k=50 мм; l=125 мм; r=225 мм; t=141 мм
- Axis-Jet-СI-450-2/4-R-300/2: 00_20_Type=Axis-Jet-СI-450-2/4-R-300/2; A=351 мм; A1=401 мм; B=500 мм; D=565 мм; D1=545 мм; D2=445 мм; Dy=450 мм; H=575 мм; Height=575 мм; L=2004 мм; L1=2129 мм; Length=2254 мм; Maximum Air Flow=9280.0 м³/ч; Motor=Motor : Motor_450; Power=1500 Вт; R=283 мм; Type R=Да; Weight=85.00 кг; Width=565 мм; d1=13 мм; dn=454 мм; k=50 мм; l=125 мм; r=225 мм; t=141 мм
- Axis-Jet-СI-450-2-R-450/2: 00_20_Type=Axis-Jet-СI-450-2-R-450/2; A=351 мм; A1=401 мм; B=500 мм; D=565 мм; D1=545 мм; D2=445 мм; Dy=450 мм; H=575 мм; Height=575 мм; L=2004 мм; L1=2129 мм; Length=2254 мм; Maximum Air Flow=8560.0 м³/ч; Motor=Motor : Motor_450; Power=1500 Вт; R=283 мм; Type R=Да; Weight=85.00 кг; Width=565 мм; d1=13 мм; dn=454 мм; k=50 мм; l=125 мм; r=225 мм; t=141 мм
- Axis-Jet-СI-450-2/4-R-400/2: 00_20_Type=Axis-Jet-СI-450-2/4-R-400/2; A=351 мм; A1=401 мм; B=500 мм; D=565 мм; D1=545 мм; D2=445 мм; Dy=450 мм; H=575 мм; Height=575 мм; L=2004 мм; L1=2129 мм; Length=2254 мм; Maximum Air Flow=8560.0 м³/ч; Motor=Motor : Motor_450; Power=1500 Вт; R=283 мм; Type R=Да; Weight=85.00 кг; Width=565 мм; d1=13 мм; dn=454 мм; k=50 мм; l=125 мм; r=225 мм; t=141 мм
- Axis-Jet-СI-450M-2-R: 00_20_Type=Axis-Jet-СI-450M-2-R; A=351 мм; A1=401 мм; B=500 мм; D=565 мм; D1=545 мм; D2=445 мм; Dy=450 мм; H=575 мм; Height=575 мм; L=2004 мм; L1=2129 мм; Length=2254 мм; Maximum Air Flow=10400.0 м³/ч; Motor=Motor : Motor_450; Power=2200 Вт; R=283 мм; Type R=Да; Weight=85.00 кг; Width=565 мм; d1=13 мм; dn=454 мм; k=50 мм; l=125 мм; r=225 мм; t=141 мм
- Axis-Jet-СI-450M-2-R-300/2: 00_20_Type=Axis-Jet-СI-450M-2-R-300/2; A=351 мм; A1=401 мм; B=500 мм; D=565 мм; D1=545 мм; D2=445 мм; Dy=450 мм; H=575 мм; Height=575 мм; L=2004 мм; L1=2129 мм; Length=2254 мм; Maximum Air Flow=10400.0 м³/ч; Motor=Motor : Motor_450; Power=2200 Вт; R=283 мм; Type R=Да; Weight=85.00 кг; Width=565 мм; d1=13 мм; dn=454 мм; k=50 мм; l=125 мм; r=225 мм; t=141 мм
- Axis-Jet-СI-450M-2/4-R: 00_20_Type=Axis-Jet-СI-450M-2/4-R; A=351 мм; A1=401 мм; B=500 мм; D=565 мм; D1=545 мм; D2=445 мм; Dy=450 мм; H=575 мм; Height=575 мм; L=2004 мм; L1=2129 мм; Length=2254 мм; Maximum Air Flow=10400.0 м³/ч; Motor=Motor : Motor_450; Power=2200 Вт; R=283 мм; Type R=Да; Weight=85.00 кг; Width=565 мм; d1=13 мм; dn=454 мм; k=50 мм; l=125 мм; r=225 мм; t=141 мм
- Axis-Jet-СI-450M-2/4-R-300/2: 00_20_Type=Axis-Jet-СI-450M-2/4-R-300/2; A=351 мм; A1=401 мм; B=500 мм; D=565 мм; D1=545 мм; D2=445 мм; Dy=450 мм; H=575 мм; Height=575 мм; L=2004 мм; L1=2129 мм; Length=2254 мм; Maximum Air Flow=10400.0 м³/ч; Motor=Motor : Motor_450; Power=2200 Вт; R=283 мм; Type R=Да; Weight=85.00 кг; Width=565 мм; d1=13 мм; dn=454 мм; k=50 мм; l=125 мм; r=225 мм; t=141 мм
- Axis-Jet-СI-450M-2-R-400/2: 00_20_Type=Axis-Jet-СI-450M-2-R-400/2; A=351 мм; A1=401 мм; B=500 мм; D=565 мм; D1=545 мм; D2=445 мм; Dy=450 мм; H=575 мм; Height=575 мм; L=2004 мм; L1=2129 мм; Length=2254 мм; Maximum Air Flow=10300.0 м³/ч; Motor=Motor : Motor_450; Power=2200 Вт; R=283 мм; Type R=Да; Weight=85.00 кг; Width=565 мм; d1=13 мм; dn=454 мм; k=50 мм; l=125 мм; r=225 мм; t=141 мм
- Axis-Jet-СI-450M-2/4-R-400/2: 00_20_Type=Axis-Jet-СI-450M-2/4-R-400/2; A=351 мм; A1=401 мм; B=500 мм; D=565 мм; D1=545 мм; D2=445 мм; Dy=450 мм; H=575 мм; Height=575 мм; L=2004 мм; L1=2129 мм; Length=2254 мм; Maximum Air Flow=10300.0 м³/ч; Motor=Motor : Motor_450; Power=2200 Вт; R=283 мм; Type R=Да; Weight=85.00 кг; Width=565 мм; d1=13 мм; dn=454 мм; k=50 мм; l=125 мм; r=225 мм; t=141 мм
- Axis-Jet-СI-450S-2-R: 00_20_Type=Axis-Jet-СI-450S-2-R; A=351 мм; A1=401 мм; B=500 мм; D=565 мм; D1=545 мм; D2=445 мм; Dy=450 мм; H=575 мм; Height=575 мм; L=2004 мм; L1=2129 мм; Length=2254 мм; Maximum Air Flow=12800.0 м³/ч; Motor=Motor : Motor_450; Power=3000 Вт; R=283 мм; Type R=Да; Weight=85.00 кг; Width=565 мм; d1=13 мм; dn=454 мм; k=50 мм; l=125 мм; r=225 мм; t=141 мм
- Axis-Jet-СI-450S-2-R-300/2: 00_20_Type=Axis-Jet-СI-450S-2-R-300/2; A=351 мм; A1=401 мм; B=500 мм; D=565 мм; D1=545 мм; D2=445 мм; Dy=450 мм; H=575 мм; Height=575 мм; L=2004 мм; L1=2129 мм; Length=2254 мм; Maximum Air Flow=12800.0 м³/ч; Motor=Motor : Motor_450; Power=3000 Вт; R=283 мм; Type R=Да; Weight=85.00 кг; Width=565 мм; d1=13 мм; dn=454 мм; k=50 мм; l=125 мм; r=225 мм; t=141 мм
- Axis-Jet-СI-450S-2/4-R: 00_20_Type=Axis-Jet-СI-450S-2-R-300/2; A=351 мм; A1=401 мм; B=500 мм; D=565 мм; D1=545 мм; D2=445 мм; Dy=450 мм; H=575 мм; Height=575 мм; L=2004 мм; L1=2129 мм; Length=2254 мм; Maximum Air Flow=12800.0 м³/ч; Motor=Motor : Motor_450; Power=3100 Вт; R=283 мм; Type R=Да; Weight=85.00 кг; Width=565 мм; d1=13 мм; dn=454 мм; k=50 мм; l=125 мм; r=225 мм; t=141 мм
- Axis-Jet-СI-450S-2/4-R-300/2: 00_20_Type=Axis-Jet-СI-450S-2/4-R-300/2; A=351 мм; A1=401 мм; B=500 мм; D=565 мм; D1=545 мм; D2=445 мм; Dy=450 мм; H=575 мм; Height=575 мм; L=2004 мм; L1=2129 мм; Length=2254 мм; Maximum Air Flow=12800.0 м³/ч; Motor=Motor : Motor_450; Power=3100 Вт; R=283 мм; Type R=Да; Weight=85.00 кг; Width=565 мм; d1=13 мм; dn=454 мм; k=50 мм; l=125 мм; r=225 мм; t=141 мм
- Axis-Jet-СI-450S-2-R-400/2: 00_20_Type=Axis-Jet-СI-450S-2-R-400/2; A=351 мм; A1=401 мм; B=500 мм; D=565 мм; D1=545 мм; D2=445 мм; Dy=450 мм; H=575 мм; Height=575 мм; L=2004 мм; L1=2129 мм; Length=2254 мм; Maximum Air Flow=11200.0 м³/ч; Motor=Motor : Motor_450; Power=3000 Вт; R=283 мм; Type R=Да; Weight=85.00 кг; Width=565 мм; d1=13 мм; dn=454 мм; k=50 мм; l=125 мм; r=225 мм; t=141 мм
- Axis-Jet-СI-450S-2/4-R-400/2: 00_20_Type=Axis-Jet-СI-450S-2/4-R-400/2; A=351 мм; A1=401 мм; B=500 мм; D=565 мм; D1=545 мм; D2=445 мм; Dy=450 мм; H=575 мм; Height=575 мм; L=2004 мм; L1=2129 мм; Length=2254 мм; Maximum Air Flow=11200.0 м³/ч; Motor=Motor : Motor_450; Power=3100 Вт; R=283 мм; Type R=Да; Weight=85.00 кг; Width=565 мм; d1=13 мм; dn=454 мм; k=50 мм; l=125 мм; r=225 мм; t=141 мм
- Axis-Jet-CI-500-2/4-U-300/2: 00_20_Type=Axis-Jet-CI-500-2/4-U-300/2; A=371 мм; A1=421 мм; B=580 мм; D=603 мм; D1=583 мм; D2=483 мм; Dy=500 мм; H=620 мм; Height=620 мм; L=2004 мм; L1=2145 мм; Length=2145 мм; Maximum Air Flow=16200.0 м³/ч; Motor=Motor : Motor_500; Power=3100 Вт; R=302 мм; Type R=Нет; Weight=110.00 кг; Width=603 мм; d1=13 мм; dn=504 мм; k=50 мм; l=141 мм; r=250 мм; t=151 мм
- Axis-Jet-CI-500-2/4-U-400/2: 00_20_Type=Axis-Jet-CI-500-2/4-U-400/2; A=371 мм; A1=421 мм; B=580 мм; D=603 мм; D1=583 мм; D2=483 мм; Dy=500 мм; H=620 мм; Height=620 мм; L=2004 мм; L1=2145 мм; Length=2145 мм; Maximum Air Flow=14900.0 м³/ч; Motor=Motor : Motor_500; Power=3100 Вт; R=302 мм; Type R=Нет; Weight=110.00 кг; Width=603 мм; d1=13 мм; dn=504 мм; k=50 мм; l=141 мм; r=250 мм; t=151 мм
- Axis-Jet-CI-500M-2/4-U: 00_20_Type=Axis-Jet-CI-500M-2/4-U; A=371 мм; A1=421 мм; B=580 мм; D=603 мм; D1=583 мм; D2=483 мм; Dy=500 мм; H=620 мм; Height=620 мм; L=2004 мм; L1=2145 мм; Length=2145 мм; Maximum Air Flow=18500.0 м³/ч; Motor=Motor : Motor_500; Power=4400 Вт; R=302 мм; Type R=Нет; Weight=110.00 кг; Width=603 мм; d1=13 мм; dn=504 мм; k=50 мм; l=141 мм; r=250 мм; t=151 мм
- Axis-Jet-CI-500M-2/4-U-300/2: 00_20_Type=Axis-Jet-CI-500M-2/4-U-300/2; A=371 мм; A1=421 мм; B=580 мм; D=603 мм; D1=583 мм; D2=483 мм; Dy=500 мм; H=620 мм; Height=620 мм; L=2004 мм; L1=2145 мм; Length=2145 мм; Maximum Air Flow=18500.0 м³/ч; Motor=Motor : Motor_500; Power=4400 Вт; R=302 мм; Type R=Нет; Weight=110.00 кг; Width=603 мм; d1=13 мм; dn=504 мм; k=50 мм; l=141 мм; r=250 мм; t=151 мм
- Axis-Jet-CI-500M-2/4-U-400/2: 00_20_Type=Axis-Jet-CI-500M-2/4-U-400/2; A=371 мм; A1=421 мм; B=580 мм; D=603 мм; D1=583 мм; D2=483 мм; Dy=500 мм; H=620 мм; Height=620 мм; L=2004 мм; L1=2145 мм; Length=2145 мм; Maximum Air Flow=17200.0 м³/ч; Motor=Motor : Motor_500; Power=4400 Вт; R=302 мм; Type R=Нет; Weight=110.00 кг; Width=603 мм; d1=13 мм; dn=504 мм; k=50 мм; l=141 мм; r=250 мм; t=151 мм
- Axis-Jet-CI-500-2/4-R-300/2: 00_20_Type=Axis-Jet-CI-500-2/4-R-300/2; A=371 мм; A1=421 мм; B=580 мм; D=603 мм; D1=583 мм; D2=483 мм; Dy=500 мм; H=620 мм; Height=620 мм; L=2004 мм; L1=2145 мм; Length=2286 мм; Maximum Air Flow=14500.0 м³/ч; Motor=Motor : Motor_500; Power=3100 Вт; R=302 мм; Type R=Да; Weight=110.00 кг; Width=603 мм; d1=13 мм; dn=504 мм; k=50 мм; l=141 мм; r=250 мм; t=151 мм
- Axis-Jet-CI-500-2/4-R-400/2: 00_20_Type=Axis-Jet-CI-500-2/4-R-400/2; A=371 мм; A1=421 мм; B=580 мм; D=603 мм; D1=583 мм; D2=483 мм; Dy=500 мм; H=620 мм; Height=620 мм; L=2004 мм; L1=2145 мм; Length=2286 мм; Maximum Air Flow=13600.0 м³/ч; Motor=Motor : Motor_500; Power=3100 Вт; R=302 мм; Type R=Да; Weight=110.00 кг; Width=603 мм; d1=13 мм; dn=504 мм; k=50 мм; l=141 мм; r=250 мм; t=151 мм
- Axis-Jet-CI-500M-2/4-R: 00_20_Type=Axis-Jet-CI-500M-2/4-R; A=371 мм; A1=421 мм; B=580 мм; D=603 мм; D1=583 мм; D2=483 мм; Dy=500 мм; H=620 мм; Height=620 мм; L=2004 мм; L1=2145 мм; Length=2286 мм; Maximum Air Flow=16600.0 м³/ч; Motor=Motor : Motor_500; Power=4400 Вт; R=302 мм; Type R=Да; Weight=110.00 кг; Width=603 мм; d1=13 мм; dn=504 мм; k=50 мм; l=141 мм; r=250 мм; t=151 мм
- Axis-Jet-CI-500M-2/4-R-300/2: 00_20_Type=Axis-Jet-CI-500M-2/4-R-300/2; A=371 мм; A1=421 мм; B=580 мм; D=603 мм; D1=583 мм; D2=483 мм; Dy=500 мм; H=620 мм; Height=620 мм; L=2004 мм; L1=2145 мм; Length=2286 мм; Maximum Air Flow=16600.0 м³/ч; Motor=Motor : Motor_500; Power=4400 Вт; R=302 мм; Type R=Да; Weight=110.00 кг; Width=603 мм; d1=13 мм; dn=504 мм; k=50 мм; l=141 мм; r=250 мм; t=151 мм
- Axis-Jet-CI-500M-2/4-R-400/2: 00_20_Type=Axis-Jet-CI-500M-2/4-R-400/2; A=371 мм; A1=421 мм; B=580 мм; D=603 мм; D1=583 мм; D2=483 мм; Dy=500 мм; H=620 мм; Height=620 мм; L=2004 мм; L1=2145 мм; Length=2286 мм; Maximum Air Flow=15900.0 м³/ч; Motor=Motor : Motor_500; Power=4400 Вт; R=302 мм; Type R=Да; Weight=110.00 кг; Width=603 мм; d1=13 мм; dn=504 мм; k=50 мм; l=141 мм; r=250 мм; t=151 мм
- Axis-Jet-CI-560-2/4-U-300/2: 00_20_Type=Axis-Jet-CI-560-2/4-U-300/2; A=446 мм; A1=496 мм; B=620 мм; D=663 мм; D1=643 мм; D2=543 мм; Dy=560 мм; H=678 мм; Height=678 мм; L=2093 мм; L1=2247 мм; Length=2247 мм; Maximum Air Flow=20200.0 м³/ч; Motor=Motor : Motor_560; Power=4400 Вт; R=332 мм; Type R=Нет; Weight=155.00 кг; Width=663 мм; d1=13 мм; dn=564 мм; k=50 мм; l=154 мм; r=280 мм; t=166 мм
- Axis-Jet-CI-560-2/4-U-400/2: 00_20_Type=Axis-Jet-CI-560-2/4-U-400/2; A=446 мм; A1=496 мм; B=620 мм; D=663 мм; D1=643 мм; D2=543 мм; Dy=560 мм; H=678 мм; Height=678 мм; L=2093 мм; L1=2247 мм; Length=2247 мм; Maximum Air Flow=18000.0 м³/ч; Motor=Motor : Motor_560; Power=4400 Вт; R=332 мм; Type R=Нет; Weight=155.00 кг; Width=663 мм; d1=13 мм; dn=564 мм; k=50 мм; l=154 мм; r=280 мм; t=166 мм
- Axis-Jet-CI-560M-2/4-U: 00_20_Type=Axis-Jet-CI-560M-2/4-U; A=446 мм; A1=496 мм; B=620 мм; D=663 мм; D1=643 мм; D2=543 мм; Dy=560 мм; H=678 мм; Height=678 мм; L=2093 мм; L1=2247 мм; Length=2247 мм; Maximum Air Flow=25100.0 м³/ч; Motor=Motor : Motor_560; Power=8000 Вт; R=332 мм; Type R=Нет; Weight=155.00 кг; Width=663 мм; d1=13 мм; dn=564 мм; k=50 мм; l=154 мм; r=280 мм; t=166 мм
- Axis-Jet-CI-560M-2/4-U-300/2: 00_20_Type=Axis-Jet-CI-560M-2/4-U-300/2; A=446 мм; A1=496 мм; B=620 мм; D=663 мм; D1=643 мм; D2=543 мм; Dy=560 мм; H=678 мм; Height=678 мм; L=2093 мм; L1=2247 мм; Length=2247 мм; Maximum Air Flow=25100.0 м³/ч; Motor=Motor : Motor_560; Power=8000 Вт; R=332 мм; Type R=Нет; Weight=155.00 кг; Width=663 мм; d1=13 мм; dn=564 мм; k=50 мм; l=154 мм; r=280 мм; t=166 мм
- Axis-Jet-CI-560M-2/4-U-400/2: 00_20_Type=Axis-Jet-CI-560M-2/4-U-400/2; A=446 мм; A1=496 мм; B=620 мм; D=663 мм; D1=643 мм; D2=543 мм; Dy=560 мм; H=678 мм; Height=678 мм; L=2093 мм; L1=2247 мм; Length=2247 мм; Maximum Air Flow=24300.0 м³/ч; Motor=Motor : Motor_560; Power=8000 Вт; R=332 мм; Type R=Нет; Weight=155.00 кг; Width=663 мм; d1=13 мм; dn=564 мм; k=50 мм; l=154 мм; r=280 мм; t=166 мм
- Axis-Jet-CI-560-2/4-R-300/2: 00_20_Type=Axis-Jet-CI-560-2/4-R-300/2; A=446 мм; A1=496 мм; B=620 мм; D=663 мм; D1=643 мм; D2=543 мм; Dy=560 мм; H=678 мм; Height=678 мм; L=2093 мм; L1=2247 мм; Length=2401 мм; Maximum Air Flow=16800.0 м³/ч; Motor=Motor : Motor_560; Power=4400 Вт; R=332 мм; Type R=Да; Weight=155.00 кг; Width=663 мм; d1=13 мм; dn=564 мм; k=50 мм; l=154 мм; r=280 мм; t=166 мм
- Axis-Jet-CI-560-2/4-R-400/2: 00_20_Type=Axis-Jet-CI-560-2/4-R-400/2; A=446 мм; A1=496 мм; B=620 мм; D=663 мм; D1=643 мм; D2=543 мм; Dy=560 мм; H=678 мм; Height=678 мм; L=2093 мм; L1=2247 мм; Length=2401 мм; Maximum Air Flow=17200.0 м³/ч; Motor=Motor : Motor_560; Power=4400 Вт; R=332 мм; Type R=Да; Weight=155.00 кг; Width=663 мм; d1=13 мм; dn=564 мм; k=50 мм; l=154 мм; r=280 мм; t=166 мм
- Axis-Jet-CI-560M-2/4-R: 00_20_Type=Axis-Jet-CI-560M-2/4-R; A=446 мм; A1=496 мм; B=620 мм; D=663 мм; D1=643 мм; D2=543 мм; Dy=560 мм; H=678 мм; Height=678 мм; L=2093 мм; L1=2247 мм; Length=2401 мм; Maximum Air Flow=21100.0 м³/ч; Motor=Motor : Motor_560; Power=6000 Вт; R=332 мм; Type R=Да; Weight=155.00 кг; Width=663 мм; d1=13 мм; dn=564 мм; k=50 мм; l=154 мм; r=280 мм; t=166 мм
- Axis-Jet-CI-560M-2/4-R-300/2: 00_20_Type=Axis-Jet-CI-560M-2/4-R-300/2; A=446 мм; A1=496 мм; B=620 мм; D=663 мм; D1=643 мм; D2=543 мм; Dy=560 мм; H=678 мм; Height=678 мм; L=2093 мм; L1=2247 мм; Length=2401 мм; Maximum Air Flow=21100.0 м³/ч; Motor=Motor : Motor_560; Power=6000 Вт; R=332 мм; Type R=Да; Weight=155.00 кг; Width=663 мм; d1=13 мм; dn=564 мм; k=50 мм; l=154 мм; r=280 мм; t=166 мм
- Axis-Jet-CI-560M-2/4-R-400/2: 00_20_Type=Axis-Jet-CI-560M-2/4-R-400/2; A=446 мм; A1=496 мм; B=620 мм; D=663 мм; D1=643 мм; D2=543 мм; Dy=560 мм; H=678 мм; Height=678 мм; L=2093 мм; L1=2247 мм; Length=2401 мм; Maximum Air Flow=18800.0 м³/ч; Motor=Motor : Motor_560; Power=6000 Вт; R=332 мм; Type R=Да; Weight=155.00 кг; Width=663 мм; d1=13 мм; dn=564 мм; k=50 мм; l=154 мм; r=280 мм; t=166 мм
- Axis-Jet-CI-630-2/4-U-300/2: 00_20_Type=Axis-Jet-CI-630-2/4-U-300/2; A=550 мм; A1=600 мм; B=710 мм; D=733 мм; D1=713 мм; D2=613 мм; Dy=630 мм; H=748 мм; Height=748 мм; L=2193 мм; L1=2357 мм; Length=2357 мм; Maximum Air Flow=31500.0 м³/ч; Motor=Motor : Motor_630; Power=12000 Вт; R=367 мм; Type R=Нет; Weight=245.00 кг; Width=733 мм; d1=13 мм; dn=634 мм; k=50 мм; l=164 мм; r=315 мм; t=183 мм
- Axis-Jet-CI-630-2/4-U-400/2: 00_20_Type=Axis-Jet-CI-630-2/4-U-400/2; A=550 мм; A1=600 мм; B=710 мм; D=733 мм; D1=713 мм; D2=613 мм; Dy=630 мм; H=748 мм; Height=748 мм; L=2193 мм; L1=2357 мм; Length=2357 мм; Maximum Air Flow=31500.0 м³/ч; Motor=Motor : Motor_630; Power=12000 Вт; R=367 мм; Type R=Нет; Weight=245.00 кг; Width=733 мм; d1=13 мм; dn=634 мм; k=50 мм; l=164 мм; r=315 мм; t=183 мм
- Axis-Jet-CI-630M-2/4-U: 00_20_Type=Axis-Jet-CI-630M-2/4-U; A=550 мм; A1=600 мм; B=710 мм; D=733 мм; D1=713 мм; D2=613 мм; Dy=630 мм; H=748 мм; Height=748 мм; L=2193 мм; L1=2357 мм; Length=2357 мм; Maximum Air Flow=35200.0 м³/ч; Motor=Motor : Motor_630; Power=16000 Вт; R=367 мм; Type R=Нет; Weight=245.00 кг; Width=733 мм; d1=13 мм; dn=634 мм; k=50 мм; l=164 мм; r=315 мм; t=183 мм
- Axis-Jet-CI-630M-2/4-U-300/2: 00_20_Type=Axis-Jet-CI-630M-2/4-U-300/2; A=550 мм; A1=600 мм; B=710 мм; D=733 мм; D1=713 мм; D2=613 мм; Dy=630 мм; H=748 мм; Height=748 мм; L=2193 мм; L1=2357 мм; Length=2357 мм; Maximum Air Flow=35200.0 м³/ч; Motor=Motor : Motor_630; Power=16000 Вт; R=367 мм; Type R=Нет; Weight=245.00 кг; Width=733 мм; d1=13 мм; dn=634 мм; k=50 мм; l=164 мм; r=315 мм; t=183 мм
- Axis-Jet-CI-630M-2/4-U-400/2: 00_20_Type=Axis-Jet-CI-630M-2/4-U-400/2; A=550 мм; A1=600 мм; B=710 мм; D=733 мм; D1=713 мм; D2=613 мм; Dy=630 мм; H=748 мм; Height=748 мм; L=2193 мм; L1=2357 мм; Length=2357 мм; Maximum Air Flow=33100.0 м³/ч; Motor=Motor : Motor_630; Power=16000 Вт; R=367 мм; Type R=Нет; Weight=245.00 кг; Width=733 мм; d1=13 мм; dn=634 мм; k=50 мм; l=164 мм; r=315 мм; t=183 мм
- Axis-Jet-CI-630-2/4-R-300/2: 00_20_Type=Axis-Jet-CI-630-2/4-R-300/2; A=550 мм; A1=600 мм; B=710 мм; D=733 мм; D1=713 мм; D2=613 мм; Dy=630 мм; H=748 мм; Height=748 мм; L=2193 мм; L1=2357 мм; Length=2521 мм; Maximum Air Flow=26700.0 м³/ч; Motor=Motor : Motor_630; Power=12000 Вт; R=367 мм; Type R=Да; Weight=245.00 кг; Width=733 мм; d1=13 мм; dn=634 мм; k=50 мм; l=164 мм; r=315 мм; t=183 мм
- Axis-Jet-CI-630-2/4-R-400/2: 00_20_Type=Axis-Jet-CI-630-2/4-R-400/2; A=550 мм; A1=600 мм; B=710 мм; D=733 мм; D1=713 мм; D2=613 мм; Dy=630 мм; H=748 мм; Height=748 мм; L=2193 мм; L1=2357 мм; Length=2521 мм; Maximum Air Flow=28800.0 м³/ч; Motor=Motor : Motor_630; Power=12000 Вт; R=367 мм; Type R=Да; Weight=245.00 кг; Width=733 мм; d1=13 мм; dn=634 мм; k=50 мм; l=164 мм; r=315 мм; t=183 мм
- Axis-Jet-CI-630M-2/4-R: 00_20_Type=Axis-Jet-CI-630M-2/4-R; A=550 мм; A1=600 мм; B=710 мм; D=733 мм; D1=713 мм; D2=613 мм; Dy=630 мм; H=748 мм; Height=748 мм; L=2193 мм; L1=2357 мм; Length=2521 мм; Maximum Air Flow=29100.0 м³/ч; Motor=Motor : Motor_630; Power=16000 Вт; R=367 мм; Type R=Да; Weight=245.00 кг; Width=733 мм; d1=13 мм; dn=634 мм; k=50 мм; l=164 мм; r=315 мм; t=183 мм
- Axis-Jet-CI-630M-2/4-R-300/2: 00_20_Type=Axis-Jet-CI-630M-2/4-R-300/2; A=550 мм; A1=600 мм; B=710 мм; D=733 мм; D1=713 мм; D2=613 мм; Dy=630 мм; H=748 мм; Height=748 мм; L=2193 мм; L1=2357 мм; Length=2521 мм; Maximum Air Flow=29100.0 м³/ч; Motor=Motor : Motor_630; Power=16000 Вт; R=367 мм; Type R=Да; Weight=245.00 кг; Width=733 мм; d1=13 мм; dn=634 мм; k=50 мм; l=164 мм; r=315 мм; t=183 мм
- Axis-Jet-CI-630M-2/4-R-400/2: 00_20_Type=Axis-Jet-CI-630M-2/4-R-400/2; A=550 мм; A1=600 мм; B=710 мм; D=733 мм; D1=713 мм; D2=613 мм; Dy=630 мм; H=748 мм; Height=748 мм; L=2193 мм; L1=2357 мм; Length=2521 мм; Maximum Air Flow=32100.0 м³/ч; Motor=Motor : Motor_630; Power=16000 Вт; R=367 мм; Type R=Да; Weight=245.00 кг; Width=733 мм; d1=13 мм; dn=634 мм; k=50 мм; l=164 мм; r=315 мм; t=183 мм
